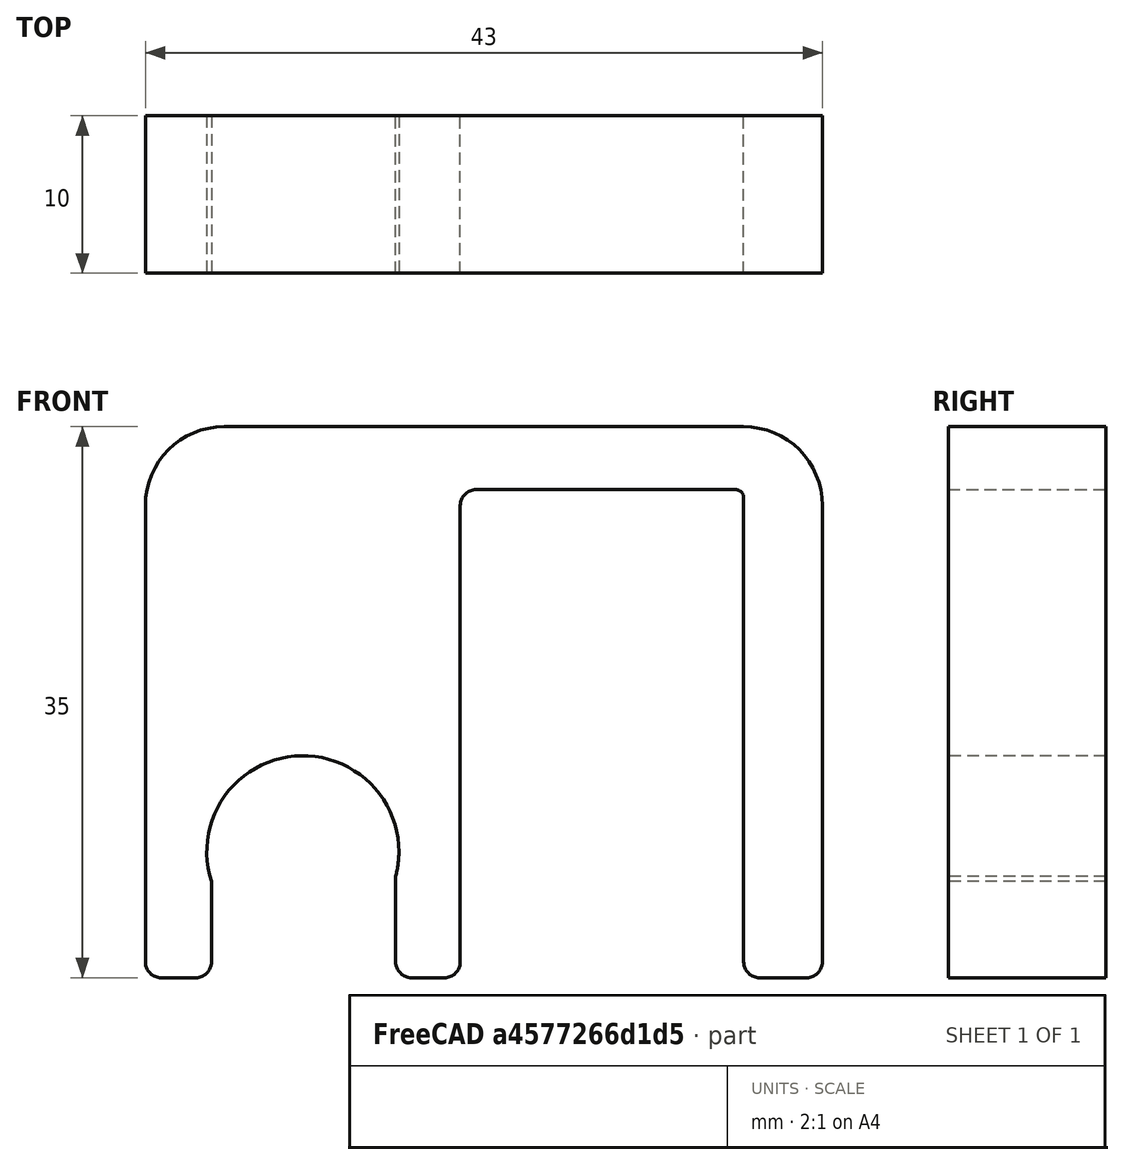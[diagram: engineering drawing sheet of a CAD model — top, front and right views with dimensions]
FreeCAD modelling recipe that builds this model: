
FCSTD DOCUMENT  (FreeCAD 0.20R24612 (Git))
Label: AbdeckungEndschalter
License: All rights reserved
LicenseURL: http://en.wikipedia.org/wiki/All_rights_reserved
objects: Part::Box×3, Part::Cut×3, Part::Fillet×3, Part::Cylinder×1
note: 10 computed .brp shape members not serialized (recipe doc carries the construction recipe); baked Part::Feature solids carry a one-line shape summary decoded from their .brp

FEATURE [Part::Cylinder] Cylinder
  Angle = 360
  AttacherType = Attacher::AttachEngine3D
  Height = 15
  Placement = pos=(10,12,8) rot=(1,0,0;1.5708rad)
  Radius = 6.1
FEATURE [Part::Box] Box002  label="Cube002"
  AttacherType = Attacher::AttachEngine3D
  Height = 35
  Length = 43
  Width = 10
FEATURE [Part::Box] Box007  label="Cube007"
  AttacherType = Attacher::AttachEngine3D
  Height = 15
  Length = 11.7
  Placement = pos=(4.2,-3,-7) rot=(0,0,1;0rad)
  Width = 15
FEATURE [Part::Box] Box  label="Cube"
  AttacherType = Attacher::AttachEngine3D
  Height = 31
  Length = 18
  Placement = pos=(20,0,0) rot=(0,0,1;0rad)
  Width = 20
FEATURE [Part::Cut] Cut
  Base = -> Box002
  Tool = -> Box
FEATURE [Part::Cut] Cut001
  Base = -> Cut
  Tool = -> Box007
FEATURE [Part::Cut] Cut002
  Base = -> Cut001
  Tool = -> Cylinder
FEATURE [Part::Fillet] Fillet
  Base = -> Cut002
  Edges = 2 edges r=5: [Edge2,Edge18]
FEATURE [Part::Fillet] Fillet001
  Base = -> Fillet
  Edges = 7 edges r=1: [Edge2,Edge22,Edge35,Edge38,Edge40,Edge41,Edge42]
FEATURE [Part::Fillet] Fillet002
  Base = -> Fillet001
  Edges = 1 edges r=0.5: [Edge55]
